# Revit family: 49010XXX
name_source: partatom
category: Plumbing Fixtures
units: mm (PartAtom-declared; Revit-internal decimal feet)

## family parameters
Always vertical = No
Cut with Voids When Loaded = No
OmniClass Number = 23.31.11.00
OmniClass Title = Faucets
Part Type = Normal
Room Calculation Point = No
Round Connector Dimension = Use Diameter
Shared = No
Work Plane-Based = Yes

## types (1)
- Default - please load Revit Family Type Catalog
    Connector Description = Water Inlet 9.5mm
    Default Elevation = 1219 mm
    Description = AXOR Citterio C Single lever basin mixer 90 with CoolStart for hand washbasins and pop-up waste set
    Diameter = 10 mm  [stored 0.0328084 ft]
    Manufacturer = AXOR
    Material = AXOR - Metal - 000 Chrome
    Model = 49010XXX
    Product Guid = 05e22ae3-d621-4d16-a4af-d02187b91070
    Product Page URL = https://www.axor-design.com
    Product data url = https://bimobject.com
    URL = https://www.axor-design.com
    Version = 1

note: [stored X ft] marks values corroborated as IEEE doubles in the binary element streams (Revit-internal decimal feet)

## geometry (parser evidence)
native form markers: Sweep x2
no freeform markers — native parametric forms only
